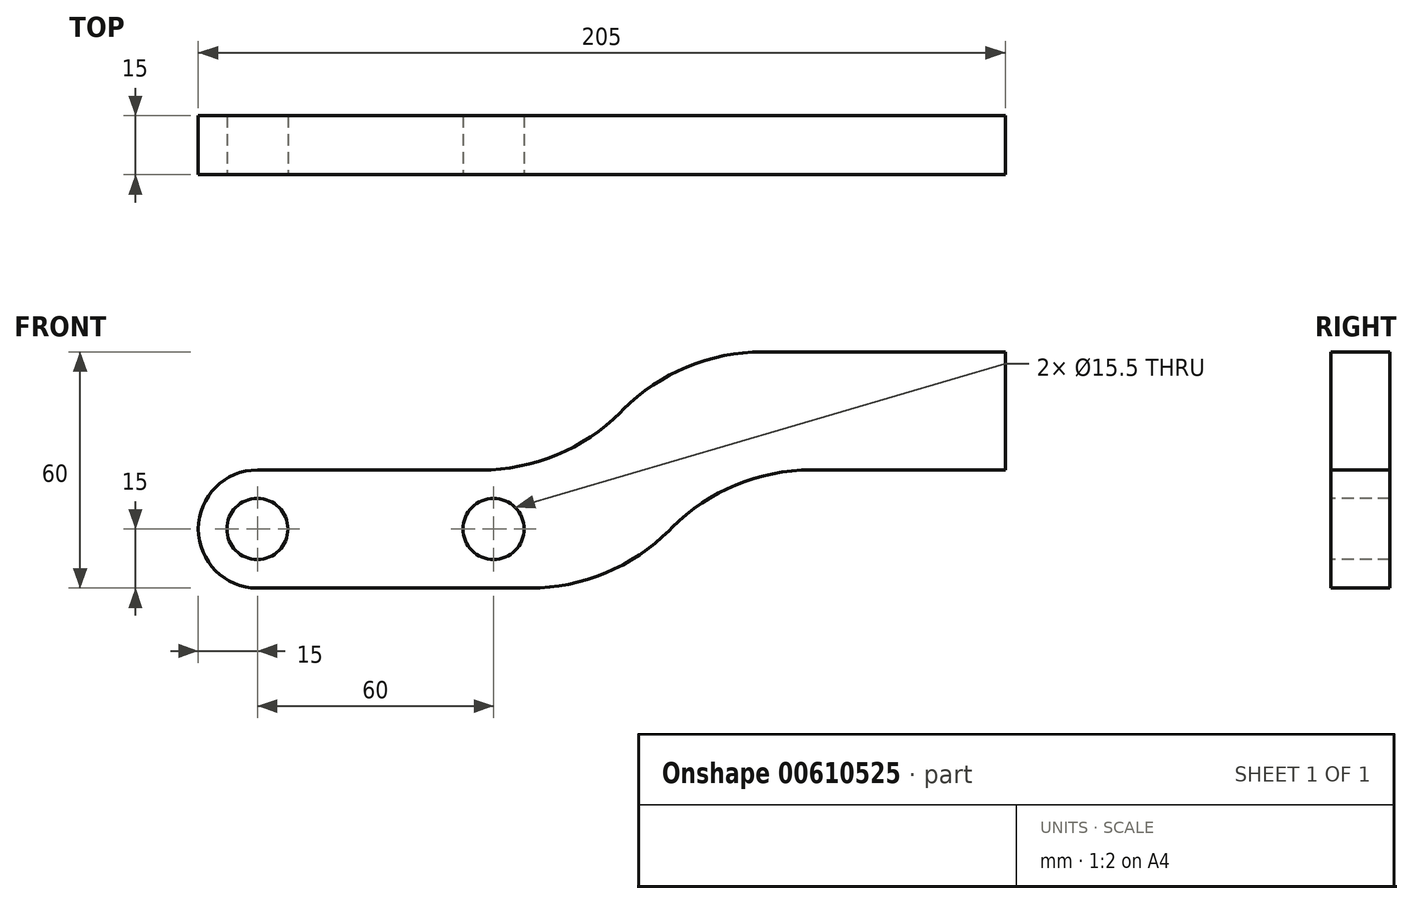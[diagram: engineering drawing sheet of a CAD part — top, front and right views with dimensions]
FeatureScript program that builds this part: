
annotation { "Feature Type Name" : "Feature", "Feature Type Description" : "" }
export const myFeature = defineFeature(function(context is Context, id is Id, definition is map)
    precondition{}
    {
        {
            var Q0;
            Q0=qCreatedBy(makeId("Front.planeOp"),FACE);
            var sketch = newSketch(context, id + "F0", { "sketchPlane" : qUnion([Q0])});
            skLineSegment(sketch, "E0", {"start": v(0, 0) * mm, "end": v(92.57, 0) * mm});
            skLineSegment(sketch, "E1", {"start": v(92.57, 0) * mm, "end": v(122.57, 30) * mm});
            skLineSegment(sketch, "E2", {"start": v(122.57, 30) * mm, "end": v(205, 30) * mm});
            skLineSegment(sketch, "E3.0", {"start": v(135, 0) * mm, "end": v(205, 0) * mm});
            skLineSegment(sketch, "E3.1", {"start": v(105, -30) * mm, "end": v(135, 0) * mm});
            skLineSegment(sketch, "E3.2", {"start": v(0, -30) * mm, "end": v(105, -30) * mm});
            skLineSegment(sketch, "E4", {"start": v(0, 0) * mm, "end": v(0, -30) * mm});
            skLineSegment(sketch, "E5", {"start": v(205, 30) * mm, "end": v(205, 0) * mm});
            skSolve(sketch);
        }
        {
            var Q0;
            Q0=makeQuery(id+"F0.imprint","IMPRINT",FACE,{"disambiguationData":[TD([[makeQuery(id+"F0.imprint","IMPRINT",EDGE,{"derivedFrom":sQuery(id+"F0.wireOp",EDGE,"E0")}),-1.0]])]});
            extrude(context, id + "F1", {"entities" : qUnion([Q0]), "endBound" : BoundingType.SYMMETRIC, "depth" : 15 * mm, "offsetDistance" : 25 * mm});
        }
        {
            var Q0;
            Q0=makeQuery(id+"F1.opExtrude","SWEPT_EDGE",EDGE,{"disambiguationData":[OSD([sQuery(id+"F0.wireOp",EDGE,"E0"),sQuery(id+"F0.wireOp",EDGE,"E1")])]});
            var Q1;
            Q1=makeQuery(id+"F1.opExtrude","SWEPT_EDGE",EDGE,{"disambiguationData":[OSD([sQuery(id+"F0.wireOp",EDGE,"E1"),sQuery(id+"F0.wireOp",EDGE,"E2")])]});
            var Q2;
            Q2=makeQuery(id+"F1.opExtrude","SWEPT_EDGE",EDGE,{"disambiguationData":[OSD([sQuery(id+"F0.wireOp",EDGE,"E3.1"),sQuery(id+"F0.wireOp",EDGE,"E3.2")])]});
            var Q3;
            Q3=makeQuery(id+"F1.opExtrude","SWEPT_EDGE",EDGE,{"disambiguationData":[OSD([sQuery(id+"F0.wireOp",EDGE,"E3.0"),sQuery(id+"F0.wireOp",EDGE,"E3.1")])]});
            fillet(context, id + "F2", {"entities" : qUnion([Q0, Q1, Q2, Q3]), "radius" : 50 * mm, "tangentPropagation" : true, "allowEdgeOverflow" : false});
        }
        {
            var Q0;
            Q0=makeQuery(id+"F1.opExtrude","SWEPT_EDGE",EDGE,{"disambiguationData":[OSD([sQuery(id+"F0.wireOp",EDGE,"E0"),sQuery(id+"F0.wireOp",EDGE,"E4")])]});
            var Q1;
            Q1=makeQuery(id+"F1.opExtrude","SWEPT_EDGE",EDGE,{"disambiguationData":[OSD([sQuery(id+"F0.wireOp",EDGE,"E3.2"),sQuery(id+"F0.wireOp",EDGE,"E4")])]});
            fillet(context, id + "F3", {"entities" : qUnion([Q0, Q1]), "radius" : 15 * mm, "tangentPropagation" : true, "allowEdgeOverflow" : false});
        }
        {
            var Q0;
            Q0=makeQuery(id+"F1.opExtrude","CAP_FACE",FACE,{"disambiguationData":[OSD([sQuery(id+"F0.wireOp",EDGE,"E0"),sQuery(id+"F0.wireOp",EDGE,"E1"),sQuery(id+"F0.wireOp",EDGE,"E2"),sQuery(id+"F0.wireOp",EDGE,"E3.0"),sQuery(id+"F0.wireOp",EDGE,"E3.1"),sQuery(id+"F0.wireOp",EDGE,"E3.2"),sQuery(id+"F0.wireOp",EDGE,"E4"),sQuery(id+"F0.wireOp",EDGE,"E5")])],"isStart":false});
            var sketch = newSketch(context, id + "F4", { "sketchPlane" : qUnion([Q0])});
            skArc(sketch, "E6.0.0", {"start": v(15, 0) * mm, "mid": v(0, -15) * mm, "end": v(15, -30) * mm, "construction": true});
            skLineSegment(sketch, "E6.0.1", {"start": v(15, -30) * mm, "end": v(84.29, -30) * mm, "construction": true});
            skArc(sketch, "E6.0.2", {"start": v(84.29, -30) * mm, "mid": v(103.42, -26.2) * mm, "end": v(119.64, -15.36) * mm, "construction": true});
            skLineSegment(sketch, "E6.0.3", {"start": v(119.64, -15.36) * mm, "end": v(120.36, -14.64) * mm, "construction": true});
            skArc(sketch, "E6.0.4", {"start": v(120.36, -14.64) * mm, "mid": v(136.58, -3.8) * mm, "end": v(155.71, 0) * mm, "construction": true});
            skLineSegment(sketch, "E6.0.5", {"start": v(155.71, 0) * mm, "end": v(205, 0) * mm, "construction": true});
            skLineSegment(sketch, "E6.0.6", {"start": v(205, 0) * mm, "end": v(205, 30) * mm, "construction": true});
            skLineSegment(sketch, "E6.0.7", {"start": v(205, 30) * mm, "end": v(143.28, 30) * mm, "construction": true});
            skArc(sketch, "E6.0.8", {"start": v(143.28, 30) * mm, "mid": v(124.15, 26.2) * mm, "end": v(107.93, 15.36) * mm, "construction": true});
            skLineSegment(sketch, "E6.0.9", {"start": v(107.93, 15.36) * mm, "end": v(107.22, 14.64) * mm, "construction": true});
            skArc(sketch, "E6.0.10", {"start": v(107.22, 14.64) * mm, "mid": v(91, 3.8) * mm, "end": v(71.86, 0) * mm, "construction": true});
            skLineSegment(sketch, "E6.0.11", {"start": v(71.86, 0) * mm, "end": v(15, 0) * mm, "construction": true});
            skLineSegment(sketch, "E7", {"start": v(0, -15) * mm, "end": v(103.48, -15) * mm, "construction": true});
            skCircle(sketch, "E8", {"center": v(15, -15) * mm, "radius": 7.75 * mm});
            skCircle(sketch, "E9", {"center": v(75, -15) * mm, "radius": 7.75 * mm});
            skSolve(sketch);
        }
        {
            var Q0;
            Q0=makeQuery(id+"F4.imprint","IMPRINT",FACE,{"disambiguationData":[TD([[makeQuery(id+"F4.imprint","IMPRINT",EDGE,{"derivedFrom":sQuery(id+"F4.wireOp",EDGE,"E8")}),1.0]])]});
            var Q1;
            Q1=makeQuery(id+"F4.imprint","IMPRINT",FACE,{"disambiguationData":[TD([[makeQuery(id+"F4.imprint","IMPRINT",EDGE,{"derivedFrom":sQuery(id+"F4.wireOp",EDGE,"E9")}),1.0]])]});
            var Q2;
            Q2=makeQuery(id+"F1.opExtrude","CAP_FACE",FACE,{"disambiguationData":[OSD([sQuery(id+"F0.wireOp",EDGE,"E0"),sQuery(id+"F0.wireOp",EDGE,"E1"),sQuery(id+"F0.wireOp",EDGE,"E2"),sQuery(id+"F0.wireOp",EDGE,"E3.0"),sQuery(id+"F0.wireOp",EDGE,"E3.1"),sQuery(id+"F0.wireOp",EDGE,"E3.2"),sQuery(id+"F0.wireOp",EDGE,"E4"),sQuery(id+"F0.wireOp",EDGE,"E5")])],"isStart":true});
            extrude(context, id + "F5", {"entities" : qUnion([Q0, Q1]), "operationType" : NewBodyOperationType.REMOVE, "endBound" : BoundingType.UP_TO_SURFACE, "oppositeDirection" : true, "depth" : 25 * mm, "endBoundEntityFace" : qUnion([Q2]), "offsetDistance" : 25 * mm});
        }
    });
